# Revit family: QF_Kelvinator_738248_KCHGM26R_1-Hinged_Glass_Door_Full_Height_Merchandiser_Refrigerator_28.5_Long
name_source: partatom
category: Specialty Equipment
units: mm (PartAtom-declared; Revit-internal decimal feet)

## family parameters
Always vertical = Yes
Cut with Voids When Loaded = No
Part Type = Normal
Room Calculation Point = No
Round Connector Dimension = Use Diameter
Shared = No
Work Plane-Based = No

## types (1)
- QF_Kelvinator_738248_KCHGM26R_1-Hinged_Glass_Door_Full_Height_Merchandiser_Refrigerator_28.5_Long
    Apparent Power = 0 VA
    Conn Conduit = Yes
    Conn Plug = 5-15P
    Cycle = 60 Hz
    Default Elevation = 0 "
    Depth = 33.701 "
    Description = Full Height Merchandiser Refrigerator 28.5" Long
    Elec Conn Connection Height = 0 "
    Elec Conn RI Height = 0 "
    FL Amps = 3 A
    Foodservice Equipment Identifier = Yes
    HP = 1/5
    Height = 83.701 "
    Identify Quantity as Lot = Yes
    Item Number = 738248
    Length = 28.346 "
    Manufacturer = Kelvinator Commercial
    Max Overcurrent Protection = 0 A
    Min Ckt Ampacity = 0 A
    Model = 738248 (KCHGM26R)
    Number of Poles = 1
    Phase = 1
    Refrigerant Type = R290
    Volts = 115 V
    Watts = 300 W
    Weight in Pounds = 348.33

## geometry (parser evidence)
native form markers: Sweep x10
no freeform markers — native parametric forms only
